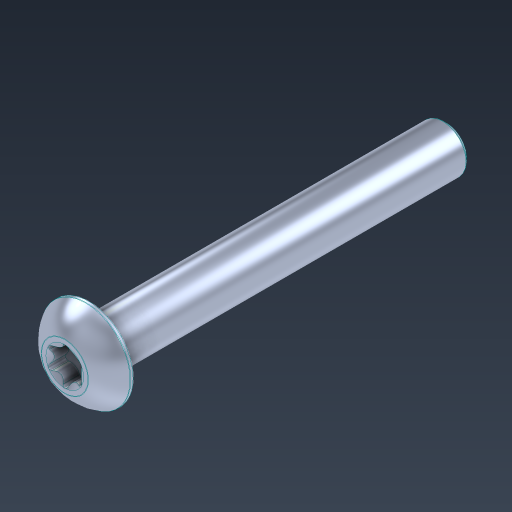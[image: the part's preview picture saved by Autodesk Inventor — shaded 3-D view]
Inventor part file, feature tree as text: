
AUTODESK INVENTOR PART (.ipt)
format: ipt  version: 2024.3 (Build 283343000, 343)  size: 187,392 bytes
history: native  units: in
note: dims shown in document units (in); Inventor stores cm internally (conversion verified against a paired STEP export)
features: fillet x1
ambient origin geometry x8: Origin, YZ Plane, XZ Plane, XY Plane, X Axis, Y Axis, Z Axis, Center Point
bodies: Solid1 (feature_tree)
feature tree (1):
  fillet  "Fillet1"  [1 undecoded]
note: 1 required parameter value undecoded (feature->parameter linkage not recoverable at this tier; creation-order binding heuristic only, values carry confidence <= 0.55)
